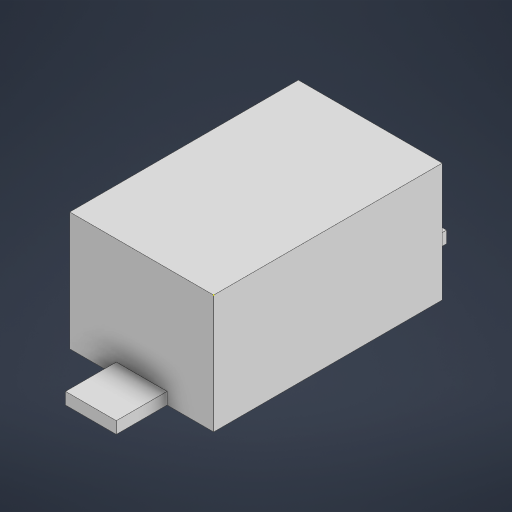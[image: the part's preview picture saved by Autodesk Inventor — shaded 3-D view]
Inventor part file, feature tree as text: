
AUTODESK INVENTOR PART (.ipt)
format: ipt  version: 2024.2 (Build 282272000, 272)  size: 174,592 bytes
history: native  units: mm
features: sketch x4, extrude x3
ambient origin geometry x8: Origin, YZ Plane, XZ Plane, XY Plane, X Axis, Y Axis, Z Axis, Center Point
bodies: Solid1 (feature_tree)
feature tree (7):
  extrude  "Extrusion1"  Depth=2.7mm
  extrude  "Extrusion2"  Depth=0.6mm
  extrude  "Extrusion3"  Depth=0.55mm
  sketch  "Sketch4"  dims[d7=0.6mm d8=0.0mm d9=0.6mm d10=0.14mm d11=0.55mm d12=1.4mm d13=0.6mm d14=0.0mm]
  sketch  "Sketch1"  dims[d0=1.7mm d1=2.7mm]
  sketch  "Sketch2"  dims[d2=1.4mm d3=0.0mm d4=0.6mm]
  sketch  "Sketch3"  dims[d5=0.14mm d6=0.55mm]
